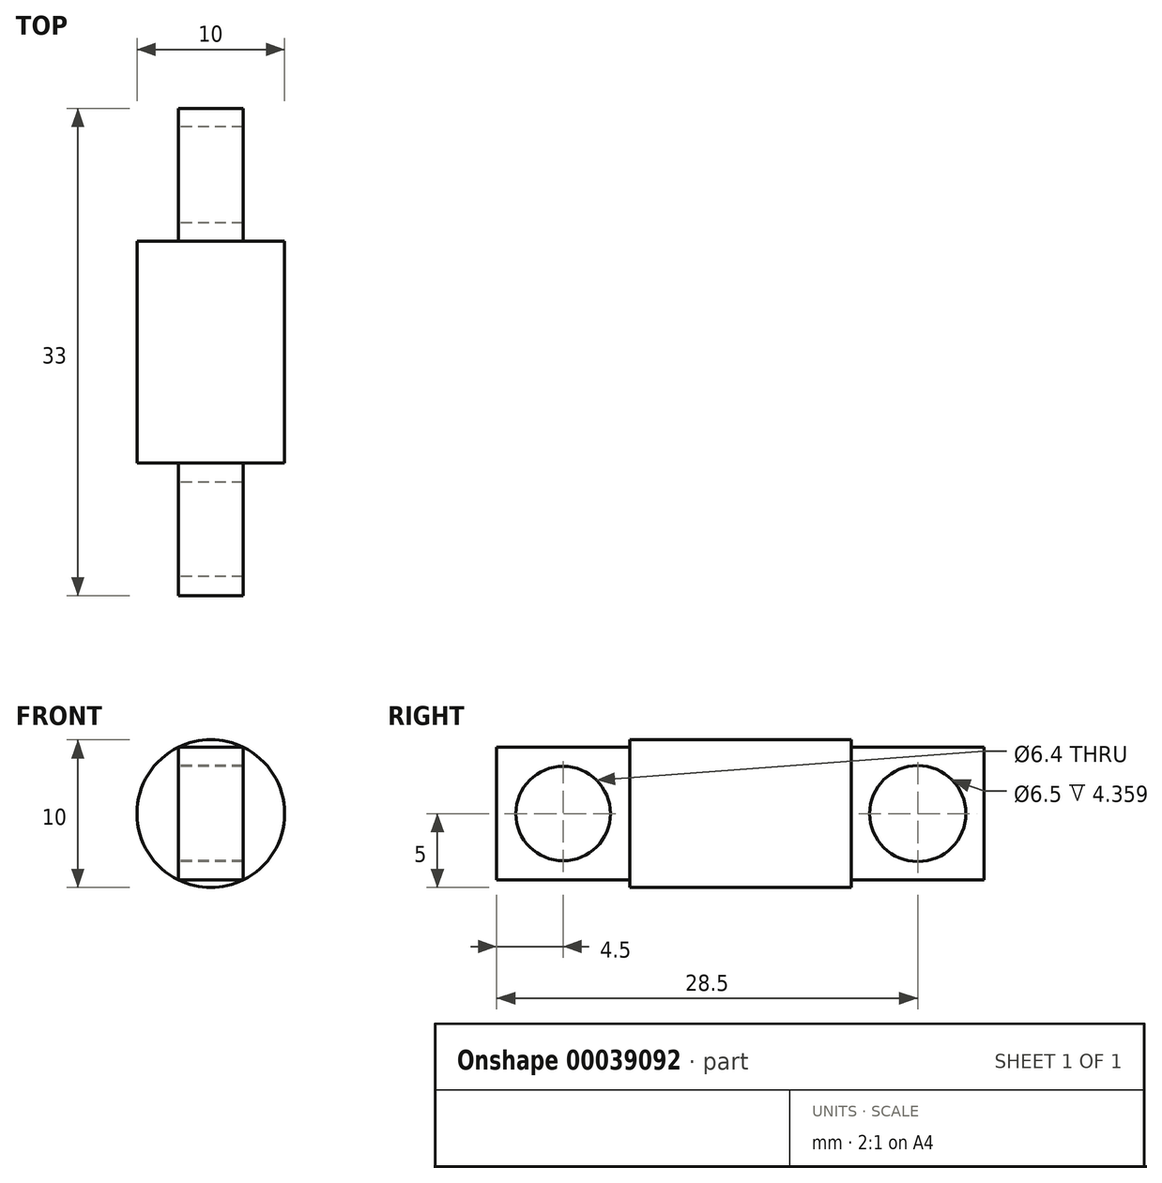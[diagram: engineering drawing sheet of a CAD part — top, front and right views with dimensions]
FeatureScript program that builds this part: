
annotation { "Feature Type Name" : "Feature", "Feature Type Description" : "" }
export const myFeature = defineFeature(function(context is Context, id is Id, definition is map)
    precondition{}
    {
        {
            var Q0;
            Q0=qCreatedBy(makeId("Top.planeOp"),FACE);
            var sketch = newSketch(context, id + "F0", { "sketchPlane" : qUnion([Q0])});
            skLineSegment(sketch, "E0.bottom", {"start": v(0, 0) * mm, "end": v(-5, 0) * mm});
            skLineSegment(sketch, "E0.top", {"start": v(0, 15) * mm, "end": v(-5, 15) * mm});
            skLineSegment(sketch, "E0.left", {"start": v(0, 0) * mm, "end": v(0, 15) * mm});
            skLineSegment(sketch, "E0.right", {"start": v(-5, 0) * mm, "end": v(-5, 15) * mm});
            skSolve(sketch);
        }
        {
            var Q0;
            Q0=makeQuery(id+"F0.imprint","IMPRINT",FACE,{"disambiguationData":[TD([[makeQuery(id+"F0.imprint","IMPRINT",EDGE,{"derivedFrom":sQuery(id+"F0.wireOp",EDGE,"E0.bottom")}),-1.0]])]});
            var Q1;
            Q1=sQuery(id+"F0.wireOp",EDGE,"E0.left");
            revolve(context, id + "F1", {"entities" : qUnion([Q0]), "axis" : qUnion([Q1]), "revolveType" : RevolveType.FULL});
        }
        {
            var Q0;
            Q0=makeQuery(id+"F1.opRevolve","SWEPT_FACE",FACE,{"disambiguationData":[OSD([sQuery(id+"F0.wireOp",EDGE,"E0.bottom")])]});
            var sketch = newSketch(context, id + "F2", { "sketchPlane" : qUnion([Q0])});
            skLineSegment(sketch, "E1.bottom", {"start": v(-2.18, 4.5) * mm, "end": v(2.18, 4.5) * mm});
            skLineSegment(sketch, "E1.top", {"start": v(-2.18, -4.5) * mm, "end": v(2.18, -4.5) * mm});
            skLineSegment(sketch, "E1.left", {"start": v(-2.18, 4.5) * mm, "end": v(-2.18, -4.5) * mm});
            skLineSegment(sketch, "E1.right", {"start": v(2.18, 4.5) * mm, "end": v(2.18, -4.5) * mm});
            skSolve(sketch);
        }
        {
            var Q0;
            Q0 = qSketchRegion(id + "F2", true);
            extrude(context, id + "F3", {"entities" : qUnion([Q0]), "operationType" : NewBodyOperationType.ADD, "depth" : 9 * mm});
        }
        {
            var Q0;
            Q0=makeQuery(id+"F3.opExtrude","SWEPT_FACE",FACE,{"disambiguationData":[OSD([sQuery(id+"F2.wireOp",EDGE,"E1.left")])]});
            var sketch = newSketch(context, id + "F4", { "sketchPlane" : qUnion([Q0])});
            skLineSegment(sketch, "E2", {"start": v(0, -4.5) * mm, "end": v(0, 4.5) * mm});
            skCircle(sketch, "E3", {"center": v(4.5, 0) * mm, "radius": 3.2 * mm});
            skSolve(sketch);
        }
        {
            var Q0;
            Q0 = qSketchRegion(id + "F4", true);
            extrude(context, id + "F5", {"entities" : qUnion([Q0]), "operationType" : NewBodyOperationType.REMOVE, "oppositeDirection" : true, "depth" : 5 * mm});
        }
        {
            var Q0;
            Q0=makeQuery(id+"F1.opRevolve","SWEPT_FACE",FACE,{"disambiguationData":[OSD([sQuery(id+"F0.wireOp",EDGE,"E0.top")])]});
            var sketch = newSketch(context, id + "F6", { "sketchPlane" : qUnion([Q0])});
            skLineSegment(sketch, "E4.bottom", {"start": v(-2.18, 4.5) * mm, "end": v(2.18, 4.5) * mm});
            skLineSegment(sketch, "E4.top", {"start": v(-2.18, -4.5) * mm, "end": v(2.18, -4.5) * mm});
            skLineSegment(sketch, "E4.left", {"start": v(-2.18, 4.5) * mm, "end": v(-2.18, -4.5) * mm});
            skLineSegment(sketch, "E4.right", {"start": v(2.18, 4.5) * mm, "end": v(2.18, -4.5) * mm});
            skSolve(sketch);
        }
        {
            var Q0;
            Q0 = qSketchRegion(id + "F6", true);
            extrude(context, id + "F7", {"entities" : qUnion([Q0]), "operationType" : NewBodyOperationType.ADD, "depth" : 9 * mm});
        }
        {
            var Q0;
            Q0=makeQuery(id+"F7.opExtrude","SWEPT_FACE",FACE,{"disambiguationData":[OSD([sQuery(id+"F6.wireOp",EDGE,"E4.right")])]});
            var sketch = newSketch(context, id + "F8", { "sketchPlane" : qUnion([Q0])});
            skCircle(sketch, "E5", {"center": v(-19.5, 0) * mm, "radius": 3.25 * mm});
            skSolve(sketch);
        }
        {
            var Q0;
            Q0 = qSketchRegion(id + "F8", true);
            extrude(context, id + "F9", {"entities" : qUnion([Q0]), "operationType" : NewBodyOperationType.REMOVE, "oppositeDirection" : true, "depth" : 5 * mm});
        }
    });
